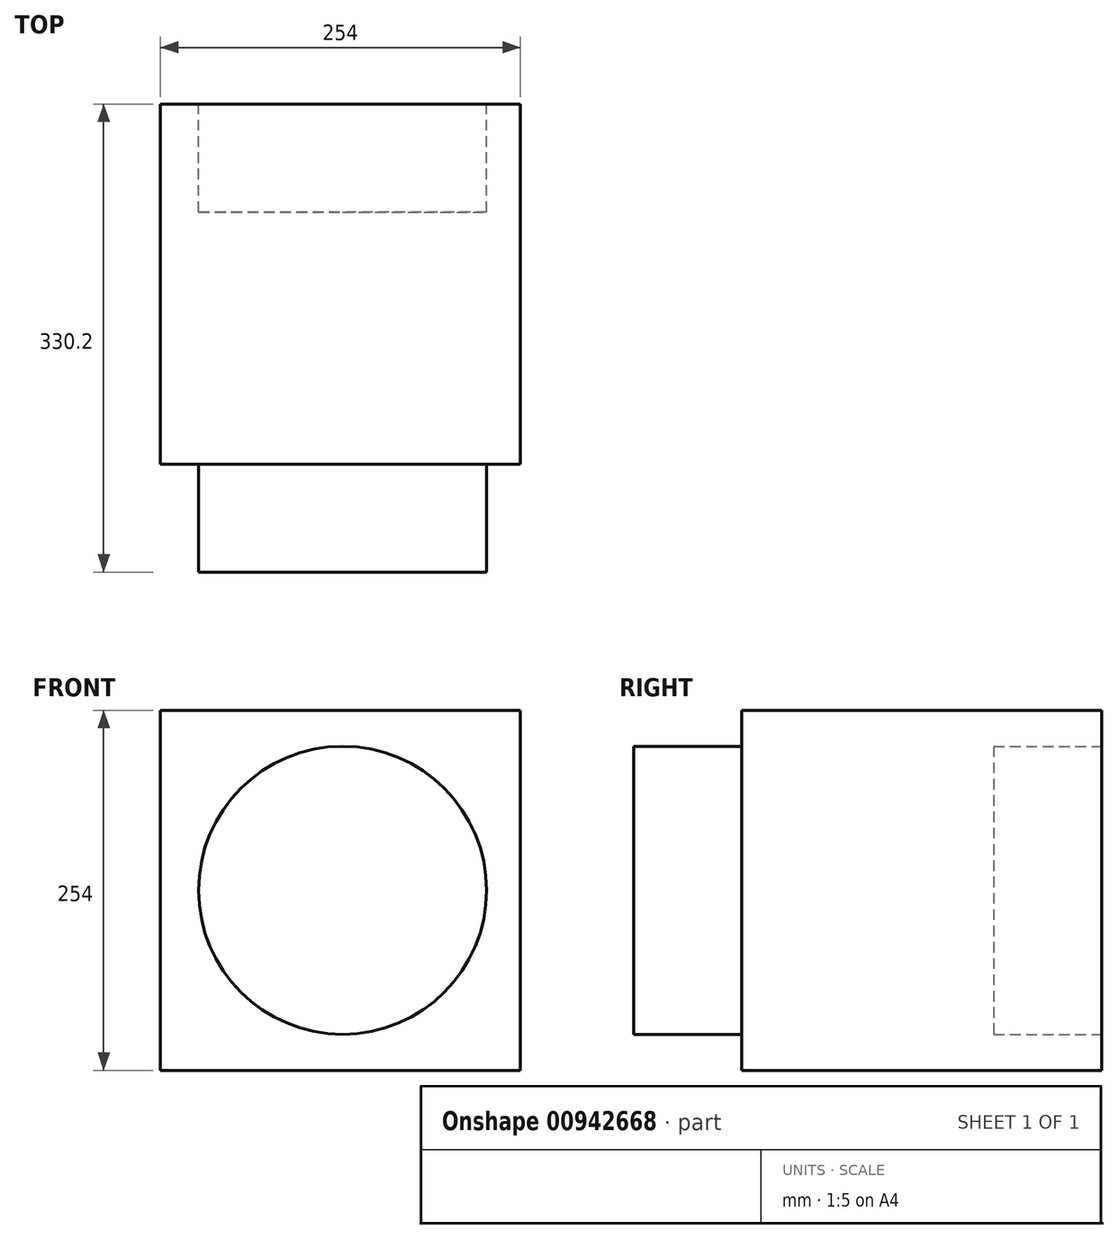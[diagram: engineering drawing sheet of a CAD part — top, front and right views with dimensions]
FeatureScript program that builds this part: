
annotation { "Feature Type Name" : "Feature", "Feature Type Description" : "" }
export const myFeature = defineFeature(function(context is Context, id is Id, definition is map)
    precondition{}
    {
        {
            var Q0;
            Q0=qCreatedBy(makeId("Top.planeOp"),FACE);
            var sketch = newSketch(context, id + "F0", { "sketchPlane" : qUnion([Q0])});
            skLineSegment(sketch, "E0.bottom", {"start": v(-128.53, 124.88) * mm, "end": v(125.47, 124.88) * mm});
            skLineSegment(sketch, "E0.top", {"start": v(-128.53, -129.12) * mm, "end": v(125.47, -129.12) * mm});
            skLineSegment(sketch, "E0.left", {"start": v(-128.53, 124.88) * mm, "end": v(-128.53, -129.12) * mm});
            skLineSegment(sketch, "E0.right", {"start": v(125.47, 124.88) * mm, "end": v(125.47, -129.12) * mm});
            skSolve(sketch);
        }
        {
            var Q0;
            Q0=makeQuery(id+"F0.imprint","IMPRINT",FACE,{"disambiguationData":[TD([[makeQuery(id+"F0.imprint","IMPRINT",EDGE,{"derivedFrom":sQuery(id+"F0.wireOp",EDGE,"E0.bottom")}),-1.0]])]});
            extrude(context, id + "F1", {"entities" : qUnion([Q0]), "depth" : 254 * mm, "offsetDistance" : 25.4 * mm});
        }
        {
            var Q0;
            Q0=makeQuery(id+"F1.opExtrude","SWEPT_FACE",FACE,{"disambiguationData":[OSD([sQuery(id+"F0.wireOp",EDGE,"E0.top")])]});
            var sketch = newSketch(context, id + "F2", { "sketchPlane" : qUnion([Q0])});
            skCircle(sketch, "E1", {"center": v(0, 127) * mm, "radius": 101.6 * mm});
            skSolve(sketch);
        }
        {
            var Q0;
            Q0=makeQuery(id+"F2.imprint","IMPRINT",FACE,{"disambiguationData":[TD([[makeQuery(id+"F2.imprint","IMPRINT",EDGE,{"derivedFrom":sQuery(id+"F2.wireOp",EDGE,"E1")}),1.0]])]});
            extrude(context, id + "F3", {"entities" : qUnion([Q0]), "operationType" : NewBodyOperationType.ADD, "depth" : 76.2 * mm, "offsetDistance" : 25.4 * mm});
        }
        {
            var Q0;
            Q0=makeQuery(id+"F1.opExtrude","SWEPT_FACE",FACE,{"disambiguationData":[OSD([sQuery(id+"F0.wireOp",EDGE,"E0.bottom")])]});
            var sketch = newSketch(context, id + "F4", { "sketchPlane" : qUnion([Q0])});
            skCircle(sketch, "E2", {"center": v(0, 127) * mm, "radius": 101.6 * mm});
            skSolve(sketch);
        }
        {
            var Q0;
            Q0=makeQuery(id+"F4.imprint","IMPRINT",FACE,{"disambiguationData":[TD([[makeQuery(id+"F4.imprint","IMPRINT",EDGE,{"derivedFrom":sQuery(id+"F4.wireOp",EDGE,"E2")}),1.0]])]});
            extrude(context, id + "F5", {"entities" : qUnion([Q0]), "operationType" : NewBodyOperationType.REMOVE, "oppositeDirection" : true, "depth" : 76.2 * mm, "offsetDistance" : 25.4 * mm});
        }
    });
